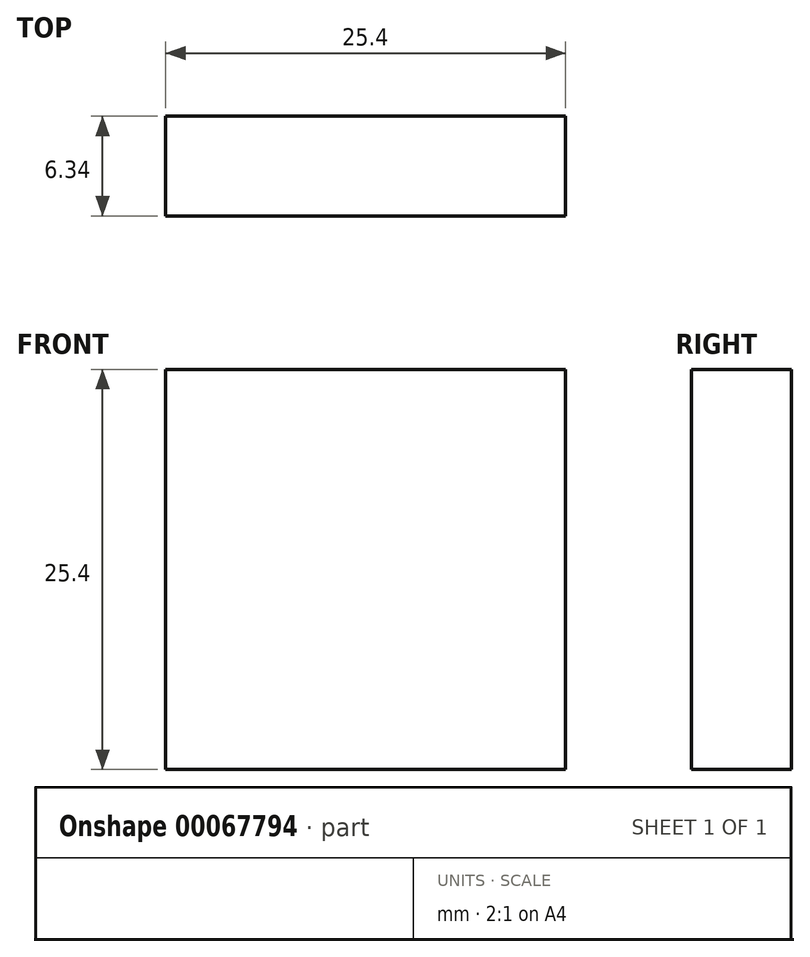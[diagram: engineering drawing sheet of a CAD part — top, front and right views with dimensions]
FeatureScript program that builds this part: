
annotation { "Feature Type Name" : "Feature", "Feature Type Description" : "" }
export const myFeature = defineFeature(function(context is Context, id is Id, definition is map)
    precondition{}
    {
        {
            var Q0;
            Q0=qCreatedBy(makeId("Front.planeOp"),FACE);
            var sketch = newSketch(context, id + "F0", { "sketchPlane" : qUnion([Q0])});
            skLineSegment(sketch, "E0.bottom", {"start": v(-12.7, 12.7) * mm, "end": v(12.7, 12.7) * mm});
            skLineSegment(sketch, "E0.top", {"start": v(-12.7, -12.7) * mm, "end": v(12.7, -12.7) * mm});
            skLineSegment(sketch, "E0.left", {"start": v(-12.7, 12.7) * mm, "end": v(-12.7, -12.7) * mm});
            skLineSegment(sketch, "E0.right", {"start": v(12.7, 12.7) * mm, "end": v(12.7, -12.7) * mm});
            skPoint(sketch, "E1", {"position": v(0, 0) * mm});
            skPoint(sketch, "E2.orphan", {"position": v(0, 12.7) * mm});
            skPoint(sketch, "E3.end.orphan", {"position": v(0, -12.7) * mm});
            skSolve(sketch);
        }
        {
            var Q0;
            Q0 = qSketchRegion(id + "F0", true);
            extrude(context, id + "F1", {"entities" : qUnion([Q0]), "endBound" : BoundingType.SYMMETRIC, "depth" : 6.35 * mm});
        }
    });
